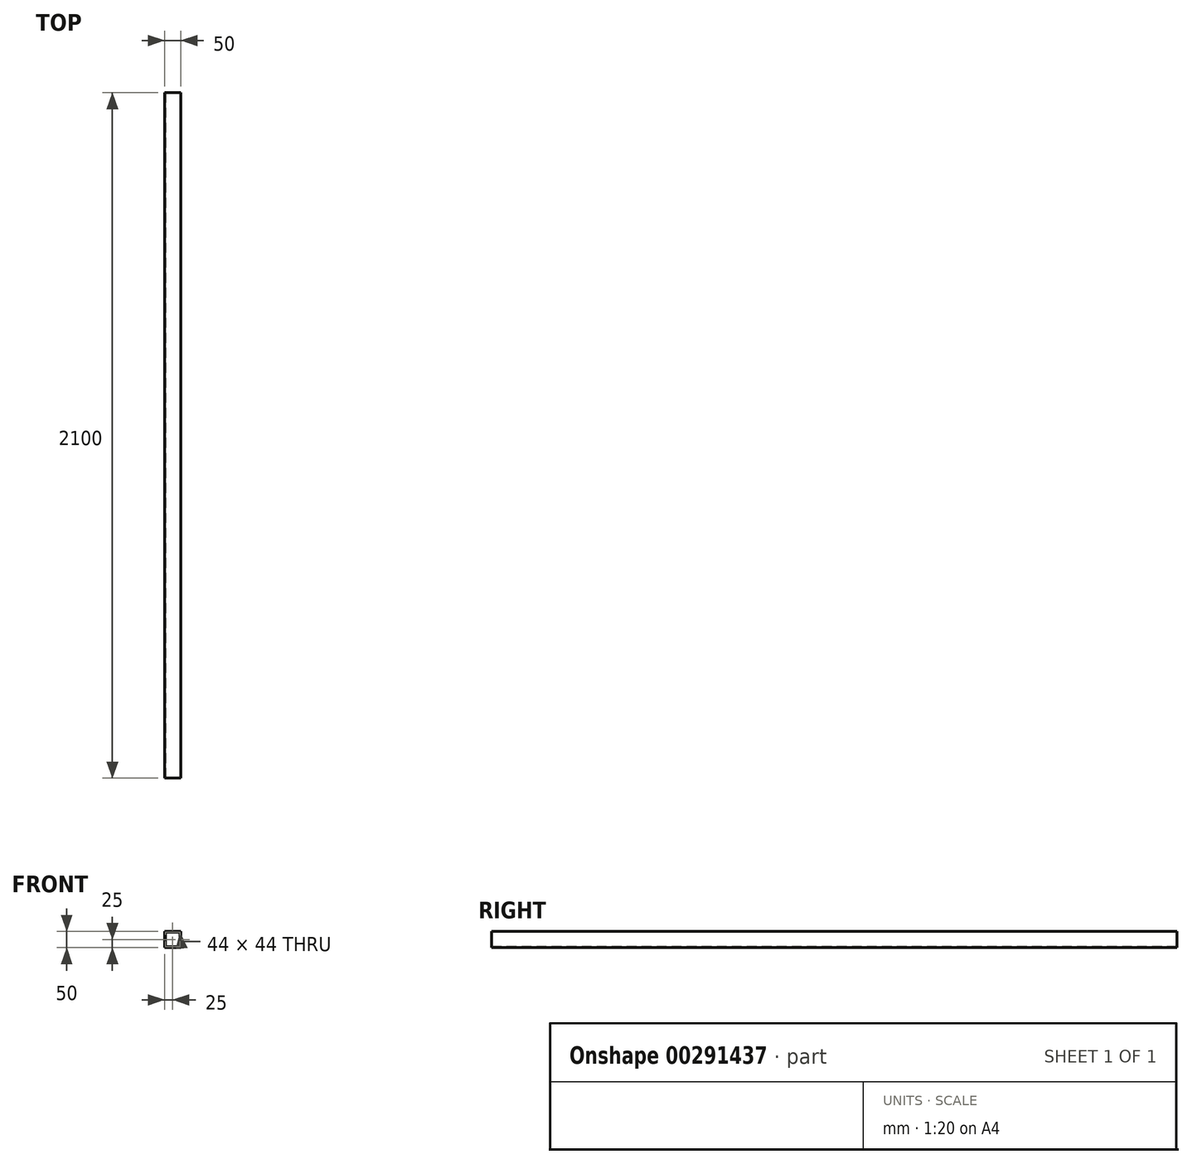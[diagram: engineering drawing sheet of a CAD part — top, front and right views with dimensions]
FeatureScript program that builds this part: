
annotation { "Feature Type Name" : "Feature", "Feature Type Description" : "" }
export const myFeature = defineFeature(function(context is Context, id is Id, definition is map)
    precondition{}
    {
        {
            var Q0;
            Q0=qCreatedBy(makeId("Front.planeOp"),FACE);
            var sketch = newSketch(context, id + "F0", { "sketchPlane" : qUnion([Q0])});
            skLineSegment(sketch, "E0.bottom", {"start": v(25, 25) * mm, "end": v(-25, 25) * mm});
            skLineSegment(sketch, "E0.top", {"start": v(25, -25) * mm, "end": v(-25, -25) * mm});
            skLineSegment(sketch, "E0.left", {"start": v(25, 25) * mm, "end": v(25, -25) * mm});
            skLineSegment(sketch, "E0.right", {"start": v(-25, 25) * mm, "end": v(-25, -25) * mm});
            skPoint(sketch, "E0.middle", {"position": v(0, 0) * mm});
            skLineSegment(sketch, "E1.0", {"start": v(22, 22) * mm, "end": v(-22, 22) * mm});
            skLineSegment(sketch, "E1.1", {"start": v(22, 22) * mm, "end": v(22, -22) * mm});
            skLineSegment(sketch, "E1.2", {"start": v(22, -22) * mm, "end": v(-22, -22) * mm});
            skLineSegment(sketch, "E1.3", {"start": v(-22, 22) * mm, "end": v(-22, -22) * mm});
            skSolve(sketch);
        }
        {
            var Q0;
            Q0=makeQuery(id+"F0.imprint","IMPRINT",FACE,{"disambiguationData":[TD([[makeQuery(id+"F0.imprint","IMPRINT",EDGE,{"derivedFrom":sQuery(id+"F0.wireOp",EDGE,"E0.bottom")}),1.0]])]});
            extrude(context, id + "F1", {"entities" : qUnion([Q0]), "oppositeDirection" : true, "depth" : 2100 * mm});
        }
    });
